# Revit family: SUPER-O
name_source: partatom
category: Plumbing Fixtures
units: mm (PartAtom-declared; Revit-internal decimal feet)

## family parameters
Always vertical = Yes
Cut with Voids When Loaded = No
OmniClass Number = 23.45.00.00
OmniClass Title = Sanitary, Laundry, and Cleaning Equipment
Part Type = Normal
Room Calculation Point = No
Round Connector Dimension = Use Diameter
Shared = No
Work Plane-Based = No

## types (7) — shared parameters
A = 111"
B = 64"
Base material = Default
C1 = 18 3/4"
Manufacturer = MIFAB
Material = Polyethylene, High Density
URL = www.mifab.com

## per-type parameters (varying)
| type | C2 | D1 | D2 | Description | E1 | E2 | Model | a |
| SUPER-500-O | 37 1/4" | 26 1/4" | 24 1/4" | 539gallon Super Max Liquid Hold Cap. Gravity Oil Interceptor | 45" | 61 1/2" | SM-MI-G-PL-500 | 8" |
| SUPER-750-O | 37 1/4" | 34 7/8" | 32 7/8" | 772gallon Super Max Liquid Hold Cap. Gravity Oil Interceptor | 53 5/8" | 70 1/8" | SM-MI-G-PL-750 | 13" |
| SUPER-1000-O | 37 1/4" | 45 1/4" | 43 1/4" | 1015gallon Super Max Liquid Hold Cap. Gravity Oil Interceptor | 64" | 80 1/2" | SM-MI-G-PL-1000 | 0" |
| SUPER-1300-O | 37 1/4" | 56 1/4" | 54 1/4" | 1312gallon Super Max Liquid Hold Cap. Gravity Oil Interceptor | 75" | 91 1/2" | SM-MI-G-PL-1300 | 0" |
| SUPER-1500-O | 37 1/4" | 64" | 62" | 1522gallon Super Max Liquid Hold Cap. Gravity Oil Interceptor | 82 3/4" | 99 1/4" | SM-MI-G-PL-1500 | 0" |
| SUPER-1250-O | 37 1/4" | 56 1/4" | 54 1/4" | 1262gallon Super Max Liquid Hold Cap. Gravity Oil Interceptor | 75" | 91 1/2" | SM-MI-G-PL-1250 | 0" |
| SUPER-2000-O | 36 1/2" | 85 1/2" | 83 1/2" | 2022gallon Super Max Liquid Hold Cap. Gravity Oil Interceptor | 104 1/4" | 120" | SM-MI-G-PL-2000 | 0" |

## geometry (parser evidence)
native form markers: Sweep x7
no freeform markers — native parametric forms only
